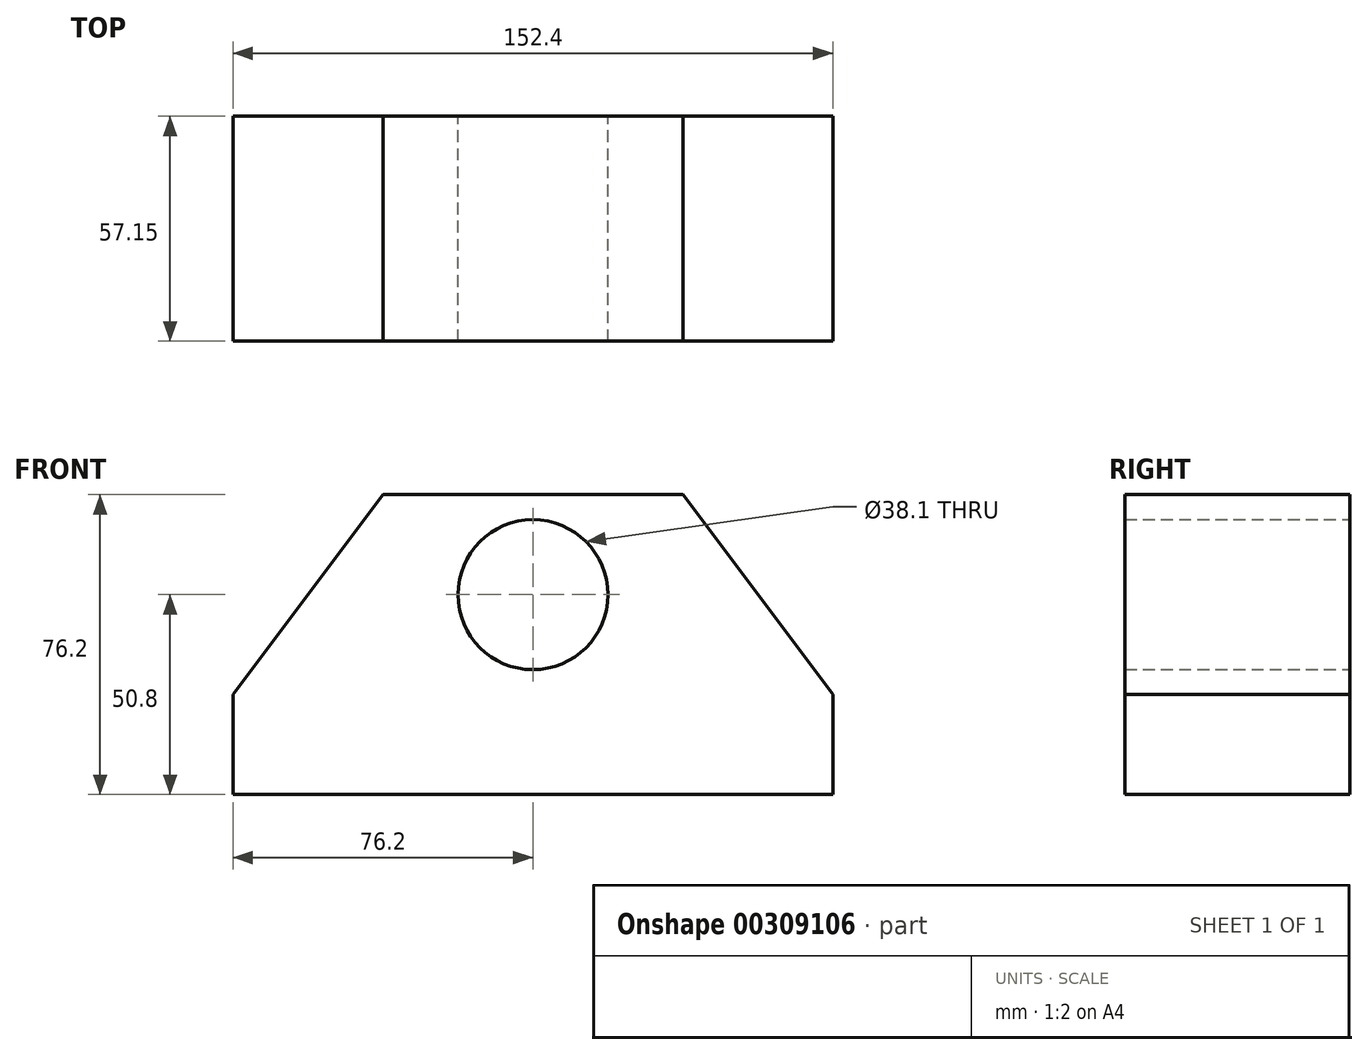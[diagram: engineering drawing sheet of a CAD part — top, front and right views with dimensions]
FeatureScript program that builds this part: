
annotation { "Feature Type Name" : "Feature", "Feature Type Description" : "" }
export const myFeature = defineFeature(function(context is Context, id is Id, definition is map)
    precondition{}
    {
        {
            var Q0;
            Q0=qCreatedBy(makeId("Front.planeOp"),FACE);
            var sketch = newSketch(context, id + "F0", { "sketchPlane" : qUnion([Q0])});
            skLineSegment(sketch, "E0", {"start": v(-67.3, 15.2) * mm, "end": v(-29.2, 66) * mm});
            skLineSegment(sketch, "E1", {"start": v(-29.2, 66) * mm, "end": v(47, 66) * mm});
            skLineSegment(sketch, "E2", {"start": v(47, 66) * mm, "end": v(85.1, 15.2) * mm});
            skLineSegment(sketch, "E3", {"start": v(85.1, 15.2) * mm, "end": v(85.1, -10.2) * mm});
            skLineSegment(sketch, "E4", {"start": v(85.1, -10.2) * mm, "end": v(-67.3, -10.2) * mm});
            skLineSegment(sketch, "E5", {"start": v(-67.3, 15.2) * mm, "end": v(-67.3, -10.2) * mm});
            skCircle(sketch, "E6", {"center": v(8.9, 40.6) * mm, "radius": 19.05 * mm});
            skSolve(sketch);
        }
        {
            var Q0;
            Q0=makeQuery(id+"F0.imprint","IMPRINT",FACE,{"disambiguationData":[TD([[makeQuery(id+"F0.imprint","IMPRINT",EDGE,{"derivedFrom":sQuery(id+"F0.wireOp",EDGE,"E0")}),-1.0]])]});
            extrude(context, id + "F1", {"entities" : qUnion([Q0]), "depth" : 57.15 * mm});
        }
    });
